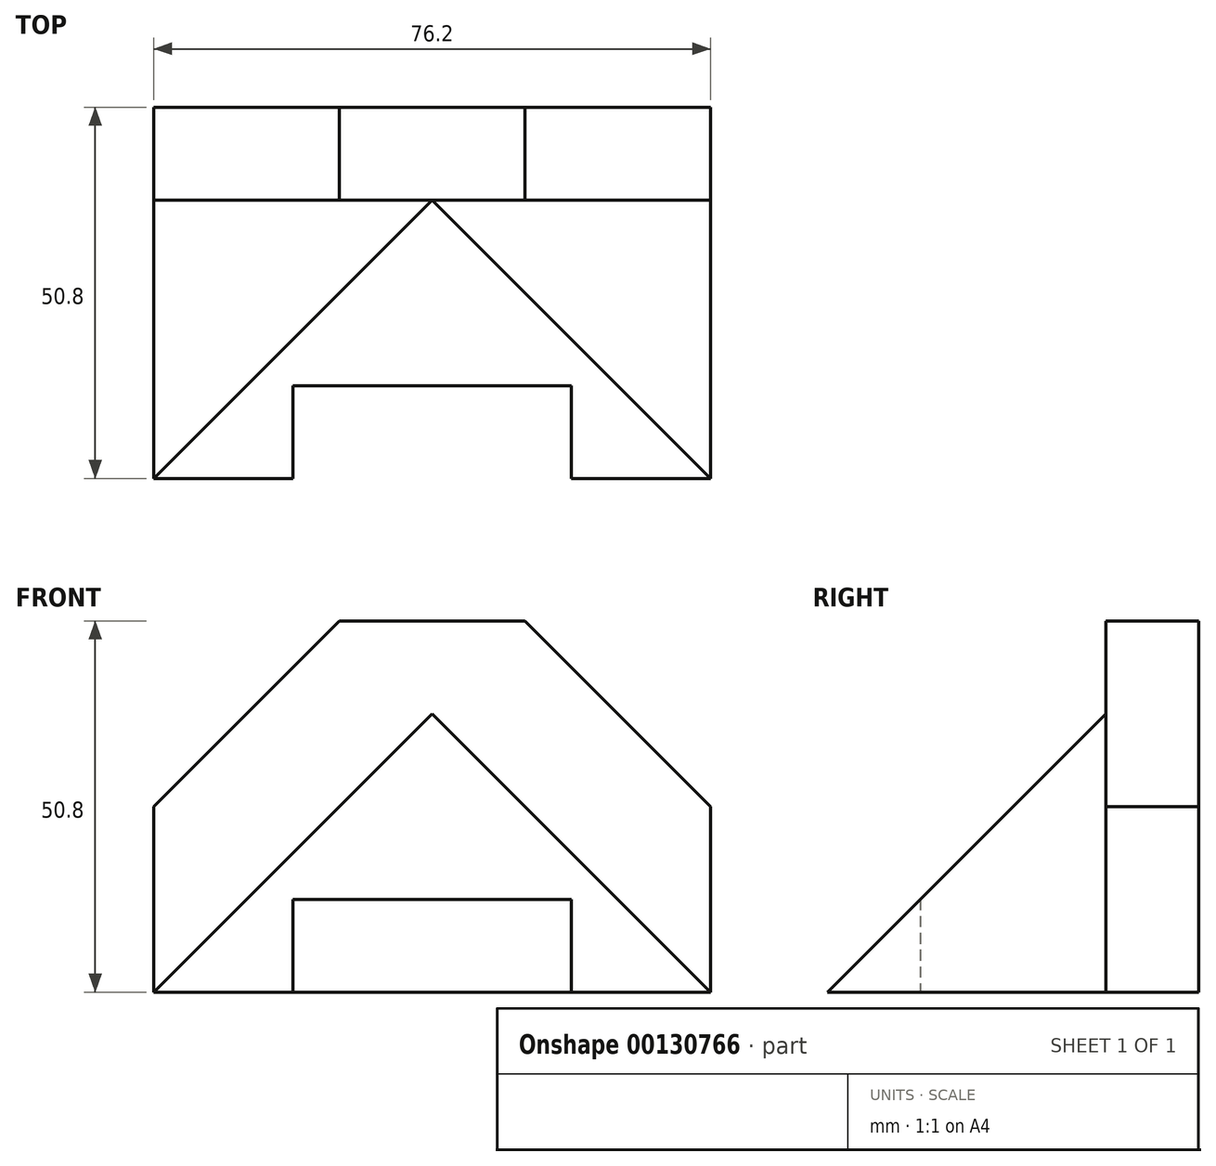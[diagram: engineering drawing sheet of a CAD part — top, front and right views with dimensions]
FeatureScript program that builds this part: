
annotation { "Feature Type Name" : "Feature", "Feature Type Description" : "" }
export const myFeature = defineFeature(function(context is Context, id is Id, definition is map)
    precondition{}
    {
        {
            var Q0;
            Q0=qCreatedBy(makeId("Front.planeOp"),FACE);
            var sketch = newSketch(context, id + "F0", { "sketchPlane" : qUnion([Q0])});
            skLineSegment(sketch, "E0", {"start": v(0, 0) * mm, "end": v(0, 25.4) * mm});
            skLineSegment(sketch, "E1", {"start": v(0, 25.4) * mm, "end": v(25.4, 50.8) * mm});
            skLineSegment(sketch, "E2", {"start": v(25.4, 50.8) * mm, "end": v(50.8, 50.8) * mm});
            skLineSegment(sketch, "E3", {"start": v(50.8, 50.8) * mm, "end": v(76.2, 25.4) * mm});
            skLineSegment(sketch, "E4", {"start": v(76.2, 25.4) * mm, "end": v(76.2, 0) * mm});
            skLineSegment(sketch, "E5", {"start": v(76.2, 0) * mm, "end": v(0, 0) * mm});
            skSolve(sketch);
        }
        {
            var Q0;
            Q0 = qSketchRegion(id + "F0", true);
            extrude(context, id + "F1", {"entities" : qUnion([Q0]), "oppositeDirection" : true, "depth" : 12.7 * mm});
        }
        {
            var Q0;
            Q0=makeQuery(id+"F1.opExtrude","CAP_FACE",FACE,{"disambiguationData":[OSD([sQuery(id+"F0.wireOp",EDGE,"E0"),sQuery(id+"F0.wireOp",EDGE,"E1"),sQuery(id+"F0.wireOp",EDGE,"E2"),sQuery(id+"F0.wireOp",EDGE,"E3"),sQuery(id+"F0.wireOp",EDGE,"E4"),sQuery(id+"F0.wireOp",EDGE,"E5")])],"isStart":true});
            var sketch = newSketch(context, id + "F2", { "sketchPlane" : qUnion([Q0])});
            skLineSegment(sketch, "E6", {"start": v(0, 0) * mm, "end": v(38.1, 38.1) * mm});
            skLineSegment(sketch, "E7", {"start": v(38.1, 38.1) * mm, "end": v(76.2, 0) * mm});
            skLineSegment(sketch, "E8", {"start": v(76.2, 0) * mm, "end": v(0, 0) * mm});
            skSolve(sketch);
        }
        {
            var Q0;
            Q0 = qSketchRegion(id + "F2", true);
            extrude(context, id + "F3", {"entities" : qUnion([Q0]), "operationType" : NewBodyOperationType.ADD, "depth" : 38.1 * mm});
        }
        {
            var Q0;
            Q0=makeQuery(id+"F1.opExtrude","SWEPT_FACE",FACE,{"disambiguationData":[OSD([sQuery(id+"F0.wireOp",EDGE,"E4")])]});
            var sketch = newSketch(context, id + "F4", { "sketchPlane" : qUnion([Q0])});
            skLineSegment(sketch, "E9", {"start": v(-38.1, 0) * mm, "end": v(0, 38.1) * mm});
            skLineSegment(sketch, "E10", {"start": v(0, 38.1) * mm, "end": v(-38.1, 38.1) * mm});
            skLineSegment(sketch, "E11", {"start": v(-38.1, 38.1) * mm, "end": v(-38.1, 0) * mm});
            skSolve(sketch);
        }
        {
            var Q0;
            Q0 = qSketchRegion(id + "F4", true);
            extrude(context, id + "F5", {"entities" : qUnion([Q0]), "operationType" : NewBodyOperationType.REMOVE, "endBound" : BoundingType.THROUGH_ALL, "oppositeDirection" : true, "depth" : 25.4 * mm});
        }
        {
            var Q0;
            Q0=makeQuery(id+"F3.boolean.opBoolean","MERGE",FACE,{"derivedFrom":[makeQuery(id+"F1.opExtrude","SWEPT_FACE",FACE,{"disambiguationData":[OSD([sQuery(id+"F0.wireOp",EDGE,"E5")])]}),makeQuery(id+"F3.opExtrude","SWEPT_FACE",FACE,{"disambiguationData":[OSD([sQuery(id+"F2.wireOp",EDGE,"E8")])]})]});
            var sketch = newSketch(context, id + "F6", { "sketchPlane" : qUnion([Q0])});
            skLineSegment(sketch, "E12", {"start": v(19.05, 38.1) * mm, "end": v(19.05, 25.4) * mm});
            skLineSegment(sketch, "E13", {"start": v(19.05, 25.4) * mm, "end": v(57.15, 25.4) * mm});
            skLineSegment(sketch, "E14", {"start": v(57.15, 25.4) * mm, "end": v(57.15, 38.1) * mm});
            skLineSegment(sketch, "E15", {"start": v(57.15, 38.1) * mm, "end": v(19.05, 38.1) * mm});
            skSolve(sketch);
        }
        {
            var Q0;
            Q0 = qSketchRegion(id + "F6", true);
            extrude(context, id + "F7", {"entities" : qUnion([Q0]), "operationType" : NewBodyOperationType.REMOVE, "endBound" : BoundingType.THROUGH_ALL, "oppositeDirection" : true, "depth" : 25.4 * mm});
        }
    });
